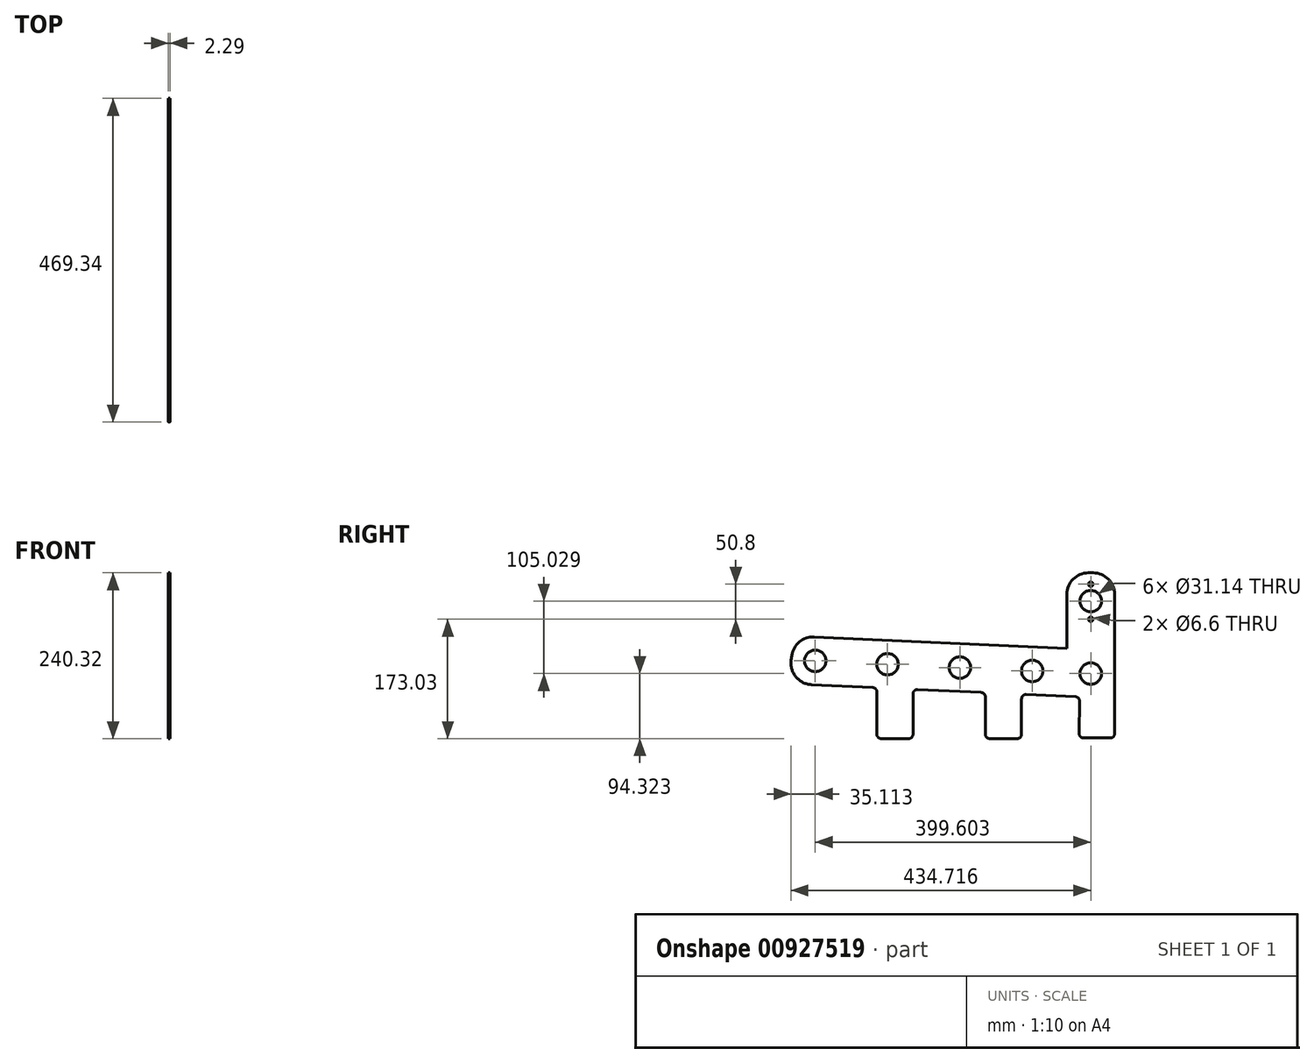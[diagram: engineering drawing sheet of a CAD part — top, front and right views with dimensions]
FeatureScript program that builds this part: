
annotation { "Feature Type Name" : "Feature", "Feature Type Description" : "" }
export const myFeature = defineFeature(function(context is Context, id is Id, definition is map)
    precondition{}
    {
        {
            var Q0;
            Q0=qCreatedBy(makeId("Right.planeOp"),FACE);
            var sketch = newSketch(context, id + "F0", { "sketchPlane" : qUnion([Q0])});
            skCircle(sketch, "E0", {"center": v(-410.1, -44.7) * mm, "radius": 15.57 * mm});
            skCircle(sketch, "E1", {"center": v(-305.18, -49.52) * mm, "radius": 15.57 * mm});
            skCircle(sketch, "E2", {"center": v(-200.26, -54.35) * mm, "radius": 15.57 * mm});
            skCircle(sketch, "E3", {"center": v(-95.34, -59.17) * mm, "radius": 15.57 * mm});
            skCircle(sketch, "E4", {"center": v(-10.5, -63.07) * mm, "radius": 15.57 * mm});
            skLineSegment(sketch, "E5", {"start": v(-411.68, -9.97) * mm, "end": v(18.07, -29.72) * mm});
            skLineSegment(sketch, "E6", {"start": v(-415.5, -79.11) * mm, "end": v(-326.8, -83.19) * mm});
            skLineSegment(sketch, "E7", {"start": v(24.13, -36.07) * mm, "end": v(24.13, -99.31) * mm});
            skPoint(sketch, "E8.visualSharp", {"position": v(-493.09, -6.23) * mm});
            skPoint(sketch, "E9.visualSharp", {"position": v(24.13, -30) * mm});
            skArc(sketch, "E9.filletArc", {"start": v(24.13, -36.07) * mm, "mid": v(22.37, -31.68) * mm, "end": v(18.07, -29.72) * mm});
            skLineSegment(sketch, "E10", {"start": v(24.13, -99.31) * mm, "end": v(24.13, -150.11) * mm});
            skLineSegment(sketch, "E11", {"start": v(-26.65, -103.14) * mm, "end": v(-27.33, -150.02) * mm});
            skLineSegment(sketch, "E12", {"start": v(-444.91, -43.74) * mm, "end": v(-443.96, -36.81) * mm});
            skLineSegment(sketch, "E13", {"start": v(18.07, -29.72) * mm, "end": v(24.13, -30) * mm});
            skLineSegment(sketch, "E14", {"start": v(24.13, -30) * mm, "end": v(24.13, -36.07) * mm});
            skPoint(sketch, "E15.visualSharp", {"position": v(-440.06, -8.67) * mm});
            skArc(sketch, "E15.filletArc", {"start": v(-411.68, -9.97) * mm, "mid": v(-433.02, -17.14) * mm, "end": v(-443.96, -36.81) * mm});
            skPoint(sketch, "E16.visualSharp", {"position": v(-449.59, -77.54) * mm});
            skArc(sketch, "E16.filletArc", {"start": v(-444.91, -43.74) * mm, "mid": v(-438, -67.91) * mm, "end": v(-415.5, -79.11) * mm});
            skCircle(sketch, "E17", {"center": v(-10.5, 41.96) * mm, "radius": 15.57 * mm});
            skLineSegment(sketch, "E18", {"start": v(-45.11, -26.82) * mm, "end": v(-45.11, 51.8) * mm});
            skLineSegment(sketch, "E19", {"start": v(24.13, -30) * mm, "end": v(24.13, 51.8) * mm});
            skLineSegment(sketch, "E20", {"start": v(-13.97, 82.93) * mm, "end": v(-7.01, 82.93) * mm});
            skCircle(sketch, "E21", {"center": v(-10.5, 66.44) * mm, "radius": 3.3 * mm});
            skCircle(sketch, "E22", {"center": v(-10.5, 15.64) * mm, "radius": 3.3 * mm});
            skPoint(sketch, "E23.visualSharp", {"position": v(-45.11, 82.93) * mm});
            skArc(sketch, "E23.filletArc", {"start": v(-13.97, 82.93) * mm, "mid": v(-36, 73.81) * mm, "end": v(-45.11, 51.8) * mm});
            skPoint(sketch, "E24.visualSharp", {"position": v(24.13, 82.93) * mm});
            skArc(sketch, "E24.filletArc", {"start": v(24.13, 51.8) * mm, "mid": v(15, 73.81) * mm, "end": v(-7.01, 82.93) * mm});
            skPoint(sketch, "E25.visualSharp", {"position": v(24.13, -150.11) * mm});
            skArc(sketch, "E25.filletArc", {"start": v(17.78, -156.46) * mm, "mid": v(22.27, -154.6) * mm, "end": v(24.13, -150.11) * mm});
            skLineSegment(sketch, "E26", {"start": v(-320.73, -89.53) * mm, "end": v(-320.73, -151.04) * mm});
            skLineSegment(sketch, "E27", {"start": v(-110.85, -99.76) * mm, "end": v(-110.85, -151.04) * mm});
            skLineSegment(sketch, "E28", {"start": v(-20.98, -156.46) * mm, "end": v(17.78, -156.46) * mm});
            skLineSegment(sketch, "E29", {"start": v(-268.22, -92.53) * mm, "end": v(-268.22, -151.04) * mm});
            skLineSegment(sketch, "E30", {"start": v(-163.36, -96.76) * mm, "end": v(-163.36, -151.04) * mm});
            skLineSegment(sketch, "E31", {"start": v(-274.57, -157.39) * mm, "end": v(-314.38, -157.39) * mm});
            skLineSegment(sketch, "E32", {"start": v(-157.01, -157.39) * mm, "end": v(-117.2, -157.39) * mm});
            skPoint(sketch, "E33.visualSharp", {"position": v(-268.22, -157.39) * mm});
            skArc(sketch, "E33.filletArc", {"start": v(-274.57, -157.39) * mm, "mid": v(-270.08, -155.53) * mm, "end": v(-268.22, -151.04) * mm});
            skPoint(sketch, "E34.visualSharp", {"position": v(-320.73, -157.39) * mm});
            skArc(sketch, "E34.filletArc", {"start": v(-320.73, -151.04) * mm, "mid": v(-318.87, -155.53) * mm, "end": v(-314.38, -157.39) * mm});
            skPoint(sketch, "E35.newPointA", {"position": v(24.13, -99.31) * mm});
            skArc(sketch, "E35.filletArc", {"start": v(-320.73, -89.53) * mm, "mid": v(-322.5, -85.14) * mm, "end": v(-326.8, -83.19) * mm});
            skLineSegment(sketch, "E36", {"start": v(-261.58, -86.18) * mm, "end": v(-169.42, -90.42) * mm});
            skPoint(sketch, "E37.visualSharp", {"position": v(-268.22, -85.88) * mm});
            skArc(sketch, "E37.filletArc", {"start": v(-261.58, -86.18) * mm, "mid": v(-266.26, -87.94) * mm, "end": v(-268.22, -92.53) * mm});
            skPoint(sketch, "E38.visualSharp", {"position": v(-163.36, -90.7) * mm});
            skArc(sketch, "E38.filletArc", {"start": v(-163.36, -96.76) * mm, "mid": v(-165.12, -92.38) * mm, "end": v(-169.42, -90.42) * mm});
            skPoint(sketch, "E39.visualSharp", {"position": v(-163.36, -157.39) * mm});
            skArc(sketch, "E39.filletArc", {"start": v(-163.36, -151.04) * mm, "mid": v(-161.5, -155.53) * mm, "end": v(-157.01, -157.39) * mm});
            skPoint(sketch, "E40.visualSharp", {"position": v(-110.85, -157.39) * mm});
            skArc(sketch, "E40.filletArc", {"start": v(-117.2, -157.39) * mm, "mid": v(-112.7, -155.53) * mm, "end": v(-110.85, -151.04) * mm});
            skLineSegment(sketch, "E41", {"start": v(-32.7, -96.7) * mm, "end": v(-104.2, -93.42) * mm});
            skArc(sketch, "E42.filletArc", {"start": v(-26.65, -103.14) * mm, "mid": v(-28.37, -98.7) * mm, "end": v(-32.7, -96.7) * mm});
            skArc(sketch, "E43.filletArc", {"start": v(-104.2, -93.42) * mm, "mid": v(-108.88, -95.17) * mm, "end": v(-110.85, -99.76) * mm});
            skPoint(sketch, "E44.visualSharp", {"position": v(-27.42, -156.46) * mm});
            skArc(sketch, "E44.filletArc", {"start": v(-27.33, -150.02) * mm, "mid": v(-25.5, -154.57) * mm, "end": v(-20.98, -156.46) * mm});
            skSolve(sketch);
        }
        {
            var Q0;
            Q0 = qSketchRegion(id + "F0", true);
            var Q1;
            Q1=makeQuery(id+"F0.imprint","IMPRINT",FACE,{"disambiguationData":[TD([[makeQuery(id+"F0.imprint","IMPRINT",EDGE,{"derivedFrom":sQuery(id+"F0.wireOp",EDGE,"NK8pLXFM-0Zj0-ySYB-kyfo-mKTtXao0ZSRH")}),-1.0]])]});
            extrude(context, id + "F1", {"entities" : qUnion([Q0, Q1]), "depth" : 2.3 * mm, "offsetDistance" : 25.4 * mm});
        }
    });
